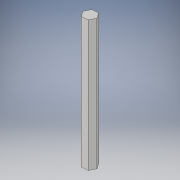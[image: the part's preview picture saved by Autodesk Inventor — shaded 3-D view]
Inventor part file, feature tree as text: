
AUTODESK INVENTOR PART (.ipt)
format: ipt  version: 2018 (Build 220112000, 112)  size: 95,232 bytes
history: native  units: in
note: dims shown in document units (in); Inventor stores cm internally (conversion verified against a paired STEP export)
features: extrude x1, sketch x1
ambient origin geometry x8: Origin, YZ Plane, XZ Plane, XY Plane, X Axis, Y Axis, Z Axis, Center Point
bodies: Solid1 (feature_tree)
feature tree (2):
  extrude  "Extrusion1"  Depth=5.0in TaperAngle=0.0deg
  sketch  "Sketch1"  dims[d1=0.5in d2=5.0in d3=0.0in]
